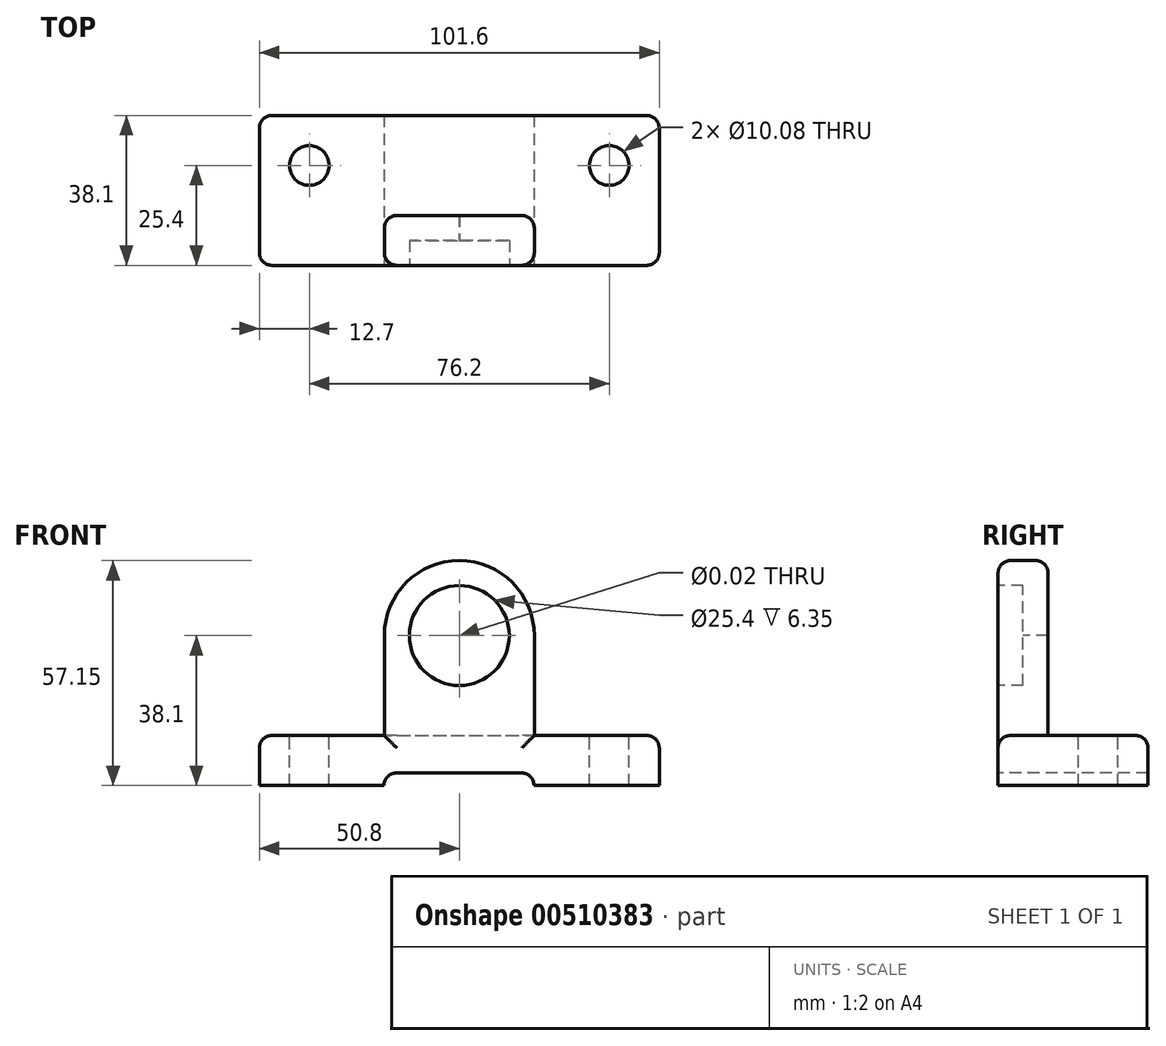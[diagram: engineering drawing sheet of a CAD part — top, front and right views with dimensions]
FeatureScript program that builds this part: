
annotation { "Feature Type Name" : "Feature", "Feature Type Description" : "" }
export const myFeature = defineFeature(function(context is Context, id is Id, definition is map)
    precondition{}
    {
        {
            var Q0;
            Q0=qCreatedBy(makeId("Top.planeOp"),FACE);
            var sketch = newSketch(context, id + "F0", { "sketchPlane" : qUnion([Q0])});
            skLineSegment(sketch, "E0.bottom", {"start": v(0, 0) * mm, "end": v(101.6, 0) * mm});
            skLineSegment(sketch, "E0.top", {"start": v(0, 38.1) * mm, "end": v(101.6, 38.1) * mm});
            skLineSegment(sketch, "E0.left", {"start": v(0, 0) * mm, "end": v(0, 38.1) * mm});
            skLineSegment(sketch, "E0.right", {"start": v(101.6, 0) * mm, "end": v(101.6, 38.1) * mm});
            skSolve(sketch);
        }
        {
            var Q0;
            Q0=makeQuery(id+"F0.imprint","IMPRINT",FACE,{"disambiguationData":[TD([[makeQuery(id+"F0.imprint","IMPRINT",EDGE,{"derivedFrom":sQuery(id+"F0.wireOp",EDGE,"E0.bottom")}),1.0]])]});
            extrude(context, id + "F1", {"entities" : qUnion([Q0]), "depth" : 12.7 * mm});
        }
        {
            var Q0;
            Q0=makeQuery(id+"F1.opExtrude","SWEPT_FACE",FACE,{"disambiguationData":[OSD([sQuery(id+"F0.wireOp",EDGE,"E0.bottom")])]});
            var sketch = newSketch(context, id + "F2", { "sketchPlane" : qUnion([Q0])});
            skLineSegment(sketch, "E1", {"start": v(31.75, 0) * mm, "end": v(31.75, 38.1) * mm});
            skArc(sketch, "E2", {"start": v(69.85, 38.1) * mm, "mid": v(50.8, 57.15) * mm, "end": v(31.75, 38.1) * mm});
            skLineSegment(sketch, "E3", {"start": v(69.85, 38.1) * mm, "end": v(69.85, 0) * mm});
            skLineSegment(sketch, "E4", {"start": v(69.85, 0) * mm, "end": v(31.75, 0) * mm});
            skSolve(sketch);
        }
        {
            var Q0;
            {var subQ0=sQuery(id+"F2.wireOp",EDGE,"E2");Q0=makeQuery(id+"F2.imprint","IMPRINT",FACE,{"disambiguationData":[TD([[makeQuery(id+"F2.imprint","IMPRINT",EDGE,{"derivedFrom":subQ0}),1.0]])]});}
            extrude(context, id + "F3", {"entities" : qUnion([Q0]), "operationType" : NewBodyOperationType.ADD, "oppositeDirection" : true, "depth" : 12.7 * mm});
        }
        {
            var Q0;
            Q0=sQuery(id+"F2.wireOp",VERTEX,"E2.center");
            var Q1;
            Q1=makeQuery(id+"F1.opExtrude","SWEPT_BODY",BODY,{"disambiguationData":[OSD([sQuery(id+"F0.wireOp",EDGE,"E0.bottom"),sQuery(id+"F0.wireOp",EDGE,"E0.top"),sQuery(id+"F0.wireOp",EDGE,"E0.left"),sQuery(id+"F0.wireOp",EDGE,"E0.right")])]});
            hole(context, id + "F4", {"style" : HoleStyle.C_BORE, "endStyle" : HoleEndStyle.THROUGH, "standardTappedOrClearance" : lookupTablePath({ "standard" : "ANSI", "size" : "15/32 (0.47)", "type" : "Drilled" }), "standardBlindInLast" : lookupTablePath({ "standard" : "ANSI", "size" : "15/32", "type" : "Drilled" }), "holeDiameter" : 15 / 812.8 * mm, "cBoreDiameter" : 25.4 * mm, "cBoreDepth" : 6.35 * mm, "isTappedThrough" : true, "tappedDepth" : 12.7 * mm, "tapClearance" : 3, "locations" : qUnion([Q0]), "scope" : qUnion([Q1])});
        }
        {
            var Q0;
            {var subQ0=sQuery(id+"F0.wireOp",EDGE,"E0.bottom");Q0=makeQuery(id+"F3.boolean.opBoolean","MERGE",FACE,{"derivedFrom":[makeQuery(id+"F1.opExtrude","SWEPT_FACE",FACE,{"disambiguationData":[OSD([subQ0])]}),makeQuery(id+"F3.opExtrude","CAP_FACE",FACE,{"disambiguationData":[OSD([subQ0,sQuery(id+"F2.wireOp",EDGE,"E1"),sQuery(id+"F2.wireOp",EDGE,"E2"),sQuery(id+"F2.wireOp",EDGE,"E3")])],"isStart":true})]});}
            var sketch = newSketch(context, id + "F5", { "sketchPlane" : qUnion([Q0])});
            skLineSegment(sketch, "E5", {"start": v(31.69, 0) * mm, "end": v(31.69, 3.17) * mm});
            skLineSegment(sketch, "E6", {"start": v(31.69, 3.17) * mm, "end": v(69.79, 3.17) * mm});
            skLineSegment(sketch, "E7", {"start": v(69.79, 3.17) * mm, "end": v(69.79, 0) * mm});
            skLineSegment(sketch, "E8", {"start": v(69.79, 0) * mm, "end": v(31.69, 0) * mm});
            skSolve(sketch);
        }
        {
            var Q0;
            Q0=makeQuery(id+"F5.imprint","IMPRINT",FACE,{"disambiguationData":[TD([[makeQuery(id+"F5.imprint","IMPRINT",EDGE,{"derivedFrom":sQuery(id+"F5.wireOp",EDGE,"E5")}),-1.0]])]});
            extrude(context, id + "F6", {"entities" : qUnion([Q0]), "operationType" : NewBodyOperationType.REMOVE, "endBound" : BoundingType.THROUGH_ALL, "oppositeDirection" : true, "depth" : 25.4 * mm});
        }
        {
            var Q0;
            Q0=makeQuery(id+"F1.opExtrude","CAP_FACE",FACE,{"disambiguationData":[OSD([sQuery(id+"F0.wireOp",EDGE,"E0.bottom"),sQuery(id+"F0.wireOp",EDGE,"E0.top"),sQuery(id+"F0.wireOp",EDGE,"E0.left"),sQuery(id+"F0.wireOp",EDGE,"E0.right")])],"isStart":false});
            var sketch = newSketch(context, id + "F7", { "sketchPlane" : qUnion([Q0])});
            skLineSegment(sketch, "E9.bottom", {"start": v(0, 38.1) * mm, "end": v(12.7, 38.1) * mm, "construction": true});
            skLineSegment(sketch, "E9.top", {"start": v(0, 25.4) * mm, "end": v(12.7, 25.4) * mm, "construction": true});
            skLineSegment(sketch, "E9.left", {"start": v(0, 38.1) * mm, "end": v(0, 25.4) * mm, "construction": true});
            skLineSegment(sketch, "E9.right", {"start": v(12.7, 38.1) * mm, "end": v(12.7, 25.4) * mm, "construction": true});
            skLineSegment(sketch, "E10.bottom", {"start": v(101.6, 38.1) * mm, "end": v(88.9, 38.1) * mm, "construction": true});
            skLineSegment(sketch, "E10.top", {"start": v(101.6, 25.4) * mm, "end": v(88.9, 25.4) * mm, "construction": true});
            skLineSegment(sketch, "E10.left", {"start": v(101.6, 38.1) * mm, "end": v(101.6, 25.4) * mm, "construction": true});
            skLineSegment(sketch, "E10.right", {"start": v(88.9, 38.1) * mm, "end": v(88.9, 25.4) * mm, "construction": true});
            skSolve(sketch);
        }
        {
            var Q0;
            Q0=sQuery(id+"F7.wireOp",VERTEX,"E9.top.end");
            var Q1;
            Q1=makeQuery(id+"F1.opExtrude","SWEPT_BODY",BODY,{"disambiguationData":[OSD([sQuery(id+"F0.wireOp",EDGE,"E0.bottom"),sQuery(id+"F0.wireOp",EDGE,"E0.top"),sQuery(id+"F0.wireOp",EDGE,"E0.left"),sQuery(id+"F0.wireOp",EDGE,"E0.right")])]});
            hole(context, id + "F8", {"style" : HoleStyle.SIMPLE, "endStyle" : HoleEndStyle.THROUGH, "standardTappedOrClearance" : lookupTablePath({ "standard" : "ANSI", "fit" : "Normal (ASME)", "size" : "3/8", "type" : "Clearance" }), "standardBlindInLast" : lookupTablePath({ "fit" : "Free", "standard" : "ANSI", "size" : "3/8", "type" : "Clearance" }), "holeDiameter" : 10.08 * mm, "isTappedThrough" : true, "tappedDepth" : 12.7 * mm, "tapClearance" : 3, "locations" : qUnion([Q0]), "scope" : qUnion([Q1])});
        }
        {
            var Q0;
            Q0=sQuery(id+"F7.wireOp",VERTEX,"E10.right.end");
            var Q1;
            Q1=makeQuery(id+"F1.opExtrude","SWEPT_BODY",BODY,{"disambiguationData":[OSD([sQuery(id+"F0.wireOp",EDGE,"E0.bottom"),sQuery(id+"F0.wireOp",EDGE,"E0.top"),sQuery(id+"F0.wireOp",EDGE,"E0.left"),sQuery(id+"F0.wireOp",EDGE,"E0.right")])]});
            hole(context, id + "F9", {"style" : HoleStyle.SIMPLE, "endStyle" : HoleEndStyle.THROUGH, "standardTappedOrClearance" : lookupTablePath({ "standard" : "ANSI", "fit" : "Normal (ASME)", "size" : "3/8", "type" : "Clearance" }), "standardBlindInLast" : lookupTablePath({ "fit" : "Free", "standard" : "ANSI", "size" : "3/8", "type" : "Clearance" }), "holeDiameter" : 10.08 * mm, "isTappedThrough" : true, "tappedDepth" : 12.7 * mm, "tapClearance" : 3, "locations" : qUnion([Q0]), "scope" : qUnion([Q1])});
        }
        {
            var Q0;
            Q0=makeQuery(id+"F3.opExtrude","CAP_EDGE",EDGE,{"disambiguationData":[OSD([sQuery(id+"F2.wireOp",EDGE,"E1")])],"isStart":true});
            var Q1;
            Q1=makeQuery(id+"F3.opExtrude","CAP_EDGE",EDGE,{"disambiguationData":[OSD([sQuery(id+"F2.wireOp",EDGE,"E1")])],"isStart":false});
            var Q2;
            Q2=makeQuery(id+"F3.opExtrude","CAP_EDGE",EDGE,{"disambiguationData":[OSD([sQuery(id+"F2.wireOp",EDGE,"E2")])],"isStart":false});
            var Q3;
            Q3=makeQuery(id+"F3.opExtrude","CAP_EDGE",EDGE,{"disambiguationData":[OSD([sQuery(id+"F2.wireOp",EDGE,"E2")])],"isStart":true});
            var Q4;
            Q4=makeQuery(id+"F3.opExtrude","CAP_EDGE",EDGE,{"disambiguationData":[OSD([sQuery(id+"F2.wireOp",EDGE,"E3")])],"isStart":true});
            var Q5;
            Q5=makeQuery(id+"F3.opExtrude","CAP_EDGE",EDGE,{"disambiguationData":[OSD([sQuery(id+"F2.wireOp",EDGE,"E3")])],"isStart":false});
            var Q6;
            Q6=makeQuery(id+"F1.opExtrude","CAP_EDGE",EDGE,{"disambiguationData":[OSD([sQuery(id+"F0.wireOp",EDGE,"E0.left")])],"isStart":false});
            var Q7;
            {var subQ1=sQuery(id+"F0.wireOp",EDGE,"E0.left");var subQ2=sQuery(id+"F0.wireOp",EDGE,"E0.bottom");Q7=makeQuery(id+"F3.boolean.opBoolean","SPLIT",EDGE,{"disambiguationData":[TD([makeQuery(id+"F1.opExtrude","SWEPT_FACE",FACE,{"disambiguationData":[OSD([subQ1])]})])],"derivedFrom":makeQuery(id+"F1.opExtrude","CAP_EDGE",EDGE,{"disambiguationData":[OSD([subQ2])],"isStart":false})});}
            var Q8;
            {var subQ1=sQuery(id+"F0.wireOp",EDGE,"E0.bottom");var subQ2=sQuery(id+"F0.wireOp",EDGE,"E0.right");Q8=makeQuery(id+"F3.boolean.opBoolean","SPLIT",EDGE,{"disambiguationData":[TD([makeQuery(id+"F1.opExtrude","SWEPT_FACE",FACE,{"disambiguationData":[OSD([subQ2])]})])],"derivedFrom":makeQuery(id+"F1.opExtrude","CAP_EDGE",EDGE,{"disambiguationData":[OSD([subQ1])],"isStart":false})});}
            var Q9;
            Q9=makeQuery(id+"F1.opExtrude","CAP_EDGE",EDGE,{"disambiguationData":[OSD([sQuery(id+"F0.wireOp",EDGE,"E0.right")])],"isStart":false});
            var Q10;
            Q10=makeQuery(id+"F1.opExtrude","CAP_EDGE",EDGE,{"disambiguationData":[OSD([sQuery(id+"F0.wireOp",EDGE,"E0.top")])],"isStart":false});
            var Q11;
            Q11=makeQuery(id+"F1.opExtrude","SWEPT_EDGE",EDGE,{"disambiguationData":[OSD([sQuery(id+"F0.wireOp",EDGE,"E0.bottom"),sQuery(id+"F0.wireOp",EDGE,"E0.right")])]});
            var Q12;
            Q12=makeQuery(id+"F1.opExtrude","SWEPT_EDGE",EDGE,{"disambiguationData":[OSD([sQuery(id+"F0.wireOp",EDGE,"E0.bottom"),sQuery(id+"F0.wireOp",EDGE,"E0.left")])]});
            var Q13;
            Q13=makeQuery(id+"F1.opExtrude","SWEPT_EDGE",EDGE,{"disambiguationData":[OSD([sQuery(id+"F0.wireOp",EDGE,"E0.top"),sQuery(id+"F0.wireOp",EDGE,"E0.left")])]});
            var Q14;
            Q14=makeQuery(id+"F1.opExtrude","SWEPT_EDGE",EDGE,{"disambiguationData":[OSD([sQuery(id+"F0.wireOp",EDGE,"E0.top"),sQuery(id+"F0.wireOp",EDGE,"E0.right")])]});
            var Q15;
            Q15=makeQuery(id+"F6.boolean.opBoolean","COPY",EDGE,{"derivedFrom":makeQuery(id+"F6.opExtrude","SWEPT_EDGE",EDGE,{"disambiguationData":[OSD([sQuery(id+"F5.wireOp",EDGE,"E6"),sQuery(id+"F5.wireOp",EDGE,"E7")])]})});
            var Q16;
            Q16=makeQuery(id+"F6.boolean.opBoolean","COPY",EDGE,{"derivedFrom":makeQuery(id+"F6.opExtrude","SWEPT_EDGE",EDGE,{"disambiguationData":[OSD([sQuery(id+"F5.wireOp",EDGE,"E5"),sQuery(id+"F5.wireOp",EDGE,"E6")])]})});
            var Q17;
            Q17=makeQuery(id+"F3.opExtrude","SWEPT_EDGE",EDGE,{"disambiguationData":[OSD([sQuery(id+"F0.wireOp",EDGE,"E0.bottom"),sQuery(id+"F2.wireOp",EDGE,"E1")])]});
            fillet(context, id + "F10", {"entities" : qUnion([Q0, Q1, Q2, Q3, Q4, Q5, Q6, Q7, Q8, Q9, Q10, Q11, Q12, Q13, Q14, Q15, Q16, Q17]), "radius" : 3.17 * mm, "tangentPropagation" : true, "allowEdgeOverflow" : false});
        }
    });
